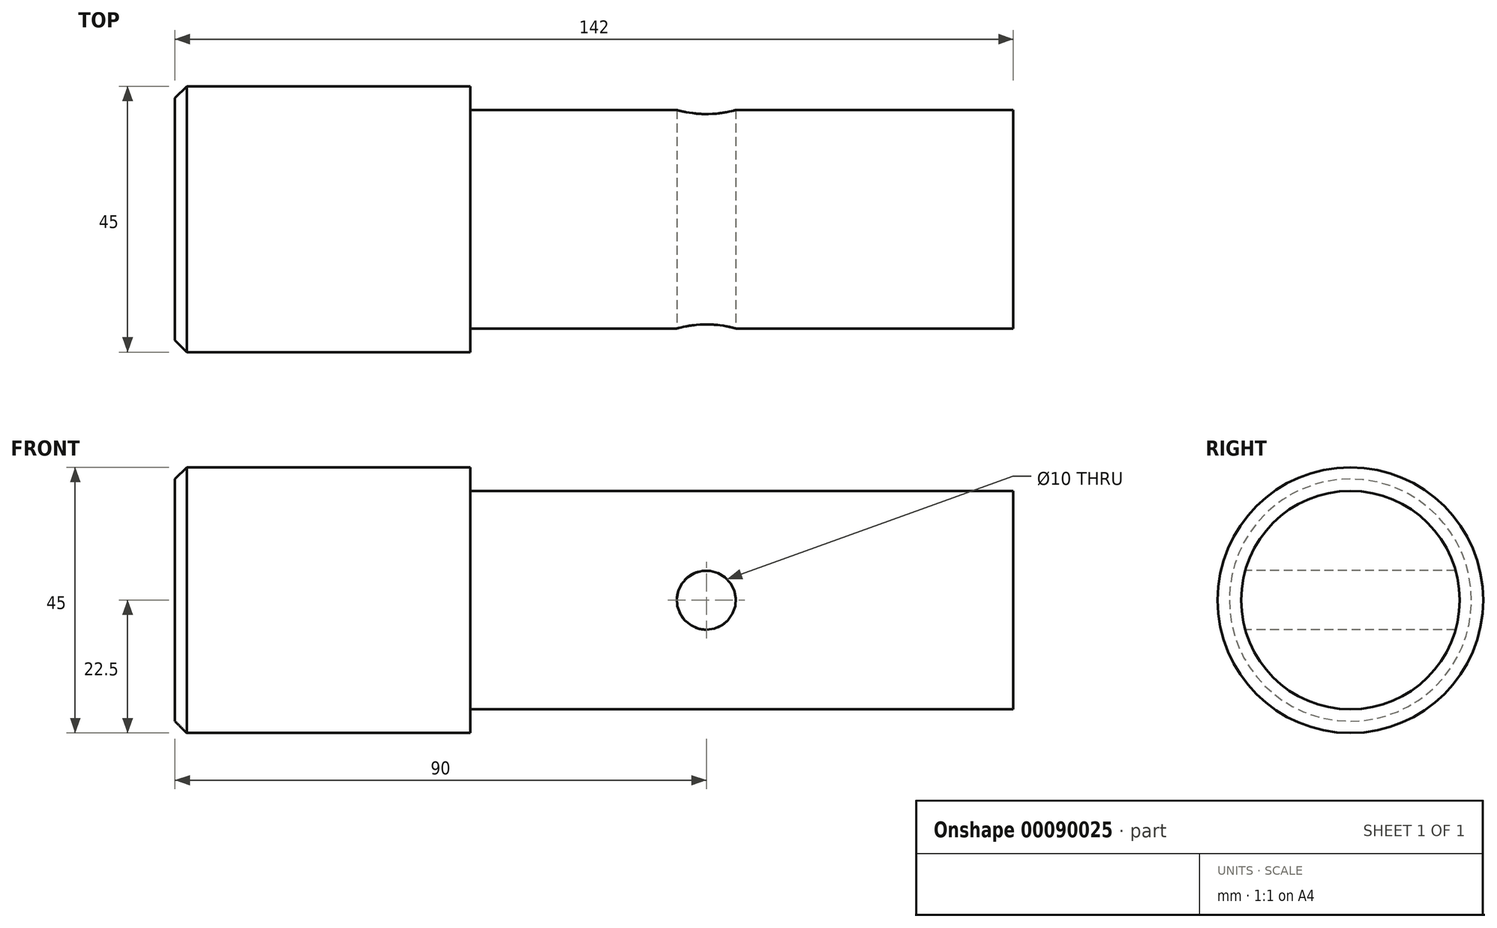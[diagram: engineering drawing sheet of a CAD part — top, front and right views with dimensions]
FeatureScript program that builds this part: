
annotation { "Feature Type Name" : "Feature", "Feature Type Description" : "" }
export const myFeature = defineFeature(function(context is Context, id is Id, definition is map)
    precondition{}
    {
        {
            var Q0;
            Q0=qCreatedBy(makeId("Right.planeOp"),FACE);
            var sketch = newSketch(context, id + "F0", { "sketchPlane" : qUnion([Q0])});
            skCircle(sketch, "E0", {"center": v(0, 0) * mm, "radius": 22.5 * mm});
            skCircle(sketch, "E1", {"center": v(0, 0) * mm, "radius": 18.5 * mm});
            skSolve(sketch);
        }
        {
            var Q0;
            Q0=makeQuery(id+"F0.imprint","IMPRINT",FACE,{"disambiguationData":[TD([[makeQuery(id+"F0.imprint","IMPRINT",EDGE,{"derivedFrom":sQuery(id+"F0.wireOp",EDGE,"E1")}),1.0]])]});
            extrude(context, id + "F1", {"entities" : qUnion([Q0]), "depth" : 142 * mm});
        }
        {
            var Q0;
            Q0=makeQuery(id+"F0.imprint","IMPRINT",FACE,{"disambiguationData":[TD([[makeQuery(id+"F0.imprint","IMPRINT",EDGE,{"derivedFrom":sQuery(id+"F0.wireOp",EDGE,"E0")}),1.0]])]});
            extrude(context, id + "F2", {"entities" : qUnion([Q0]), "operationType" : NewBodyOperationType.ADD, "depth" : 50 * mm});
        }
        {
            var Q0;
            Q0=qCreatedBy(makeId("Front.planeOp"),FACE);
            var sketch = newSketch(context, id + "F3", { "sketchPlane" : qUnion([Q0])});
            skCircle(sketch, "E2", {"center": v(90, 0) * mm, "radius": 5 * mm});
            skSolve(sketch);
        }
        {
            var Q0;
            Q0 = qSketchRegion(id + "F3", true);
            extrude(context, id + "F4", {"entities" : qUnion([Q0]), "operationType" : NewBodyOperationType.REMOVE, "oppositeDirection" : true, "depth" : 50 * mm, "symmetric" : true});
        }
        {
            var Q0;
            Q0=makeQuery(id+"F2.opExtrude","CAP_EDGE",EDGE,{"disambiguationData":[OSD([sQuery(id+"F0.wireOp",EDGE,"E0")])],"isStart":true});
            chamfer(context, id + "F5", {"entities" : qUnion([Q0]), "width" : 2 * mm, "tangentPropagation" : true});
        }
    });
